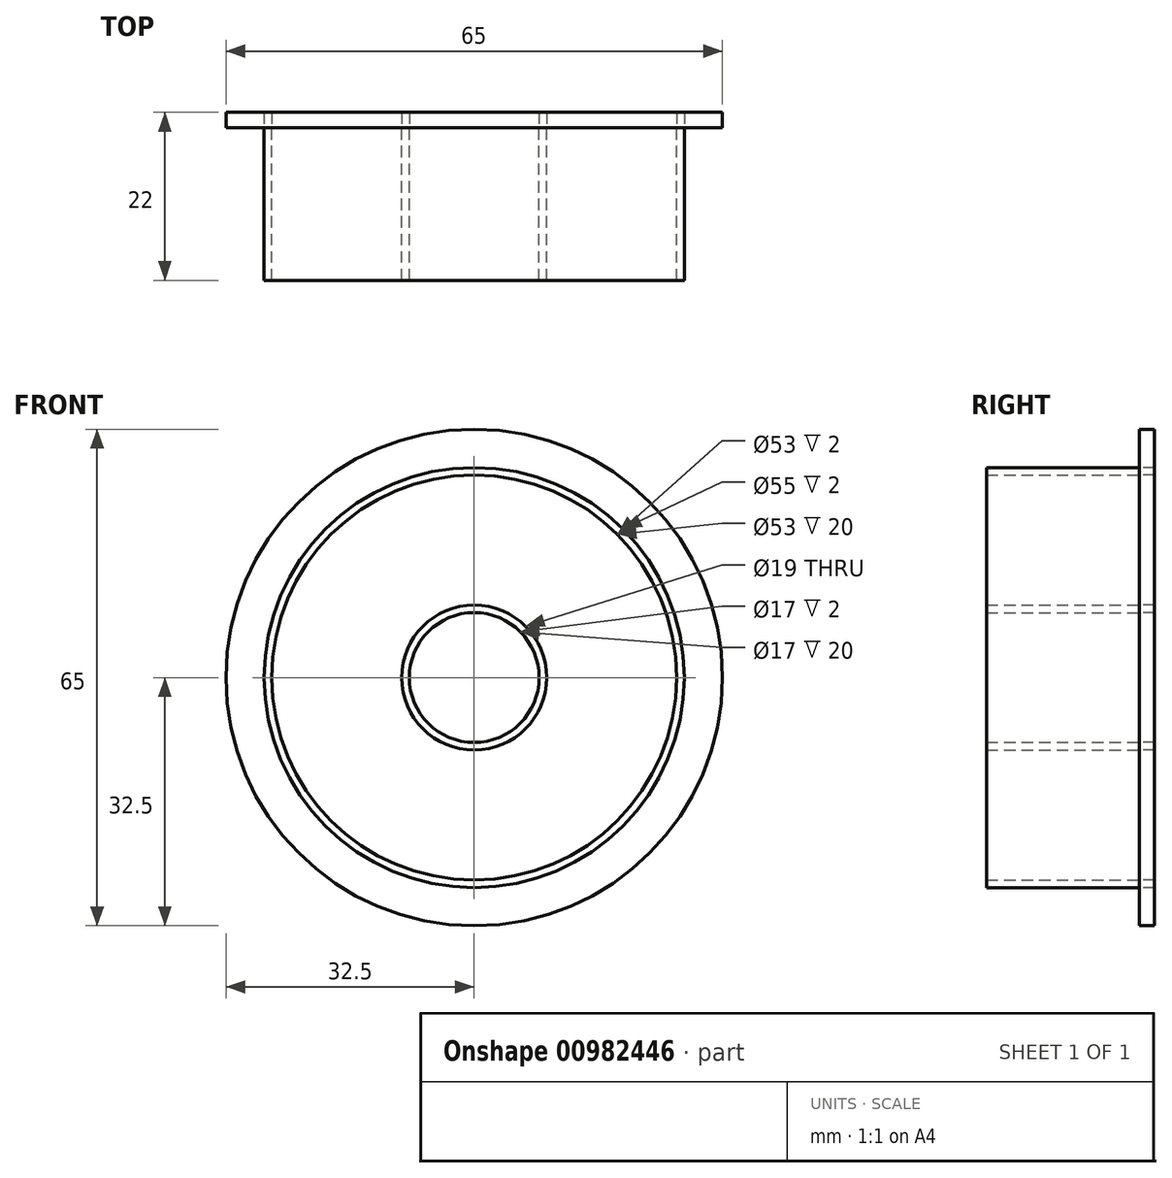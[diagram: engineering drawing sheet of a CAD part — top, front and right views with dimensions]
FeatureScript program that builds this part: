
annotation { "Feature Type Name" : "Feature", "Feature Type Description" : "" }
export const myFeature = defineFeature(function(context is Context, id is Id, definition is map)
    precondition{}
    {
        {
            var Q0;
            Q0=qCreatedBy(makeId("Front.planeOp"),FACE);
            var sketch = newSketch(context, id + "F0", { "sketchPlane" : qUnion([Q0])});
            skCircle(sketch, "E0", {"center": v(0, 0) * mm, "radius": 8.5 * mm});
            skCircle(sketch, "E1", {"center": v(0, 0) * mm, "radius": 9.5 * mm});
            skCircle(sketch, "E2", {"center": v(0, 0) * mm, "radius": 27.5 * mm});
            skCircle(sketch, "E3", {"center": v(0, 0) * mm, "radius": 26.5 * mm});
            skCircle(sketch, "E4", {"center": v(0, 0) * mm, "radius": 32.5 * mm});
            skSolve(sketch);
        }
        {
            var Q0;
            Q0=makeQuery(id+"F0.imprint","IMPRINT",FACE,{"disambiguationData":[TD([[makeQuery(id+"F0.imprint","IMPRINT",EDGE,{"derivedFrom":sQuery(id+"F0.wireOp",EDGE,"E0")}),-1.0]])]});
            var Q1;
            Q1=makeQuery(id+"F0.imprint","IMPRINT",FACE,{"disambiguationData":[TD([[makeQuery(id+"F0.imprint","IMPRINT",EDGE,{"derivedFrom":sQuery(id+"F0.wireOp",EDGE,"E2")}),1.0]])]});
            extrude(context, id + "F1", {"entities" : qUnion([Q0, Q1]), "depth" : 20 * mm, "offsetDistance" : 25 * mm});
        }
        {
            var Q0;
            Q0=makeQuery(id+"F0.imprint","IMPRINT",FACE,{"disambiguationData":[TD([[makeQuery(id+"F0.imprint","IMPRINT",EDGE,{"derivedFrom":sQuery(id+"F0.wireOp",EDGE,"E2")}),-1.0]])]});
            var Q1;
            Q1=makeQuery(id+"F0.imprint","IMPRINT",FACE,{"disambiguationData":[TD([[makeQuery(id+"F0.imprint","IMPRINT",EDGE,{"derivedFrom":sQuery(id+"F0.wireOp",EDGE,"E1")}),-1.0]])]});
            var Q2;
            Q2=makeQuery(id+"F1.opExtrude","CAP_FACE",FACE,{"disambiguationData":[OSD([sQuery(id+"F0.wireOp",EDGE,"E2"),sQuery(id+"F0.wireOp",EDGE,"E3")])],"isStart":true});
            var Q3;
            Q3=makeQuery(id+"F1.opExtrude","CAP_FACE",FACE,{"disambiguationData":[OSD([sQuery(id+"F0.wireOp",EDGE,"E0"),sQuery(id+"F0.wireOp",EDGE,"E1")])],"isStart":true});
            extrude(context, id + "F2", {"entities" : qUnion([Q0, Q1, Q2, Q3]), "oppositeDirection" : true, "depth" : 2 * mm, "offsetDistance" : 25 * mm});
        }
    });
